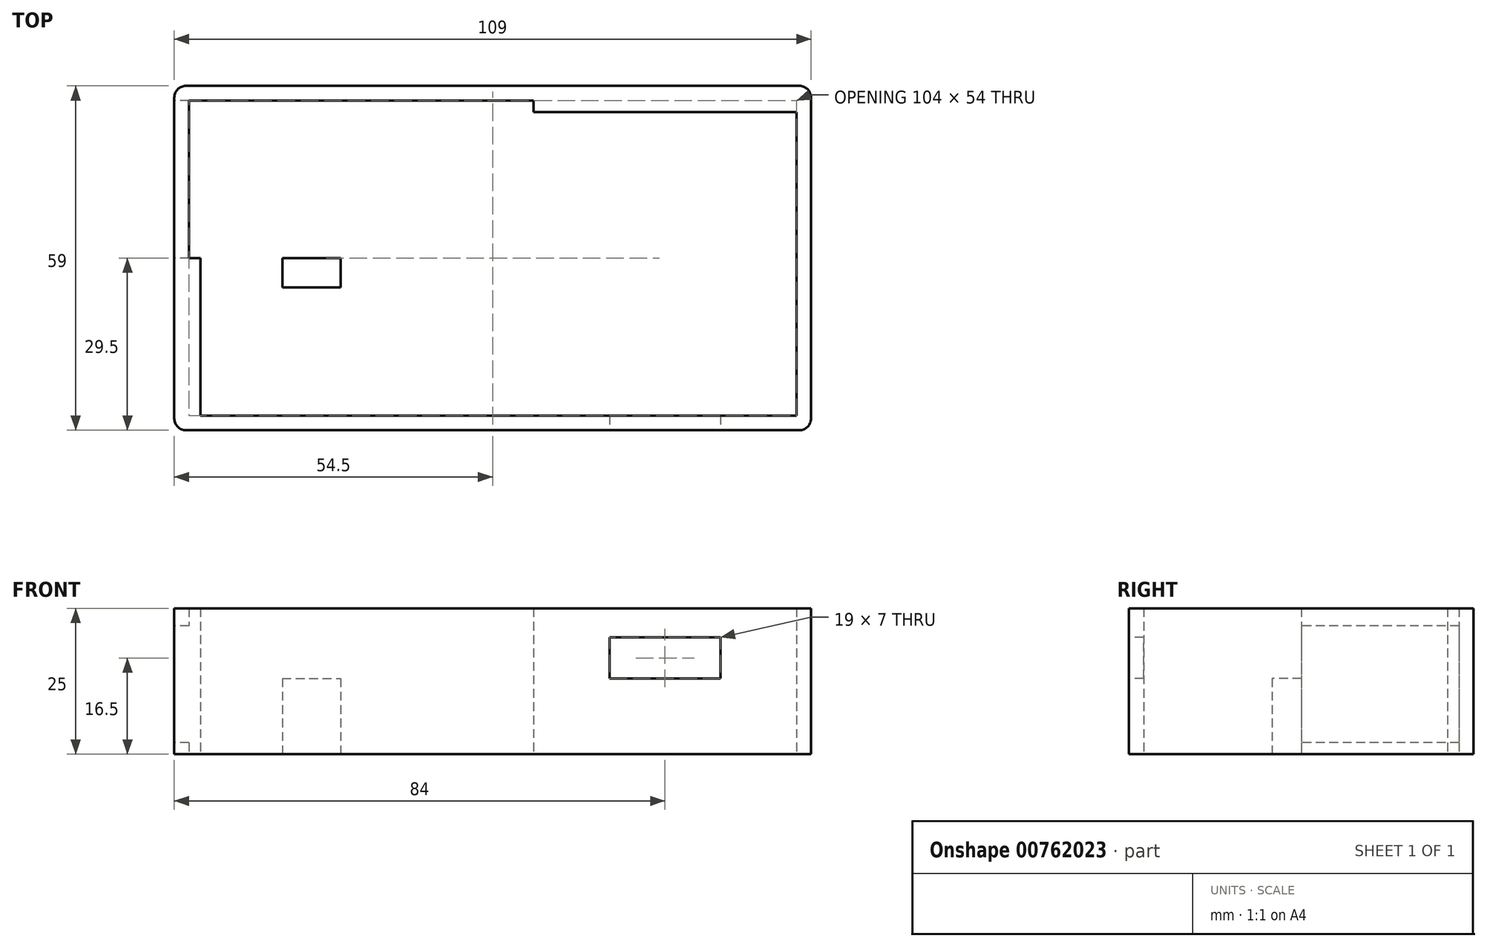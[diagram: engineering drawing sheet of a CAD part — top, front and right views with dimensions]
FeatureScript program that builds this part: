
annotation { "Feature Type Name" : "Feature", "Feature Type Description" : "" }
export const myFeature = defineFeature(function(context is Context, id is Id, definition is map)
    precondition{}
    {
        {
            var Q0;
            Q0=qCreatedBy(makeId("Top.planeOp"),FACE);
            var sketch = newSketch(context, id + "F0", { "sketchPlane" : qUnion([Q0])});
            skLineSegment(sketch, "E0.bottom", {"start": v(2, 0) * mm, "end": v(107, 0) * mm});
            skLineSegment(sketch, "E0.top", {"start": v(2, 59) * mm, "end": v(107, 59) * mm});
            skLineSegment(sketch, "E0.left", {"start": v(0, 2) * mm, "end": v(0, 57) * mm});
            skLineSegment(sketch, "E0.right", {"start": v(109, 2) * mm, "end": v(109, 57) * mm});
            skPoint(sketch, "E1.visualSharp", {"position": v(109, 59) * mm});
            skArc(sketch, "E1.filletArc", {"start": v(109, 57) * mm, "mid": v(108.41, 58.41) * mm, "end": v(107, 59) * mm});
            skPoint(sketch, "E2.visualSharp", {"position": v(109, 0) * mm});
            skArc(sketch, "E2.filletArc", {"start": v(107, 0) * mm, "mid": v(108.41, 0.59) * mm, "end": v(109, 2) * mm});
            skPoint(sketch, "E3.visualSharp", {"position": v(0, 0) * mm});
            skArc(sketch, "E3.filletArc", {"start": v(0, 2) * mm, "mid": v(0.59, 0.59) * mm, "end": v(2, 0) * mm});
            skPoint(sketch, "E4.visualSharp", {"position": v(0, 59) * mm});
            skArc(sketch, "E4.filletArc", {"start": v(2, 59) * mm, "mid": v(0.59, 58.41) * mm, "end": v(0, 57) * mm});
            skLineSegment(sketch, "E5.0", {"start": v(2.5, 56.5) * mm, "end": v(106.5, 56.5) * mm});
            skLineSegment(sketch, "E5.1", {"start": v(2.5, 2.5) * mm, "end": v(2.5, 56.5) * mm});
            skLineSegment(sketch, "E5.2", {"start": v(2.5, 2.5) * mm, "end": v(106.5, 2.5) * mm});
            skLineSegment(sketch, "E5.3", {"start": v(106.5, 2.5) * mm, "end": v(106.5, 56.5) * mm});
            skLineSegment(sketch, "E6.bottom", {"start": v(106.5, 56.5) * mm, "end": v(61.5, 56.5) * mm});
            skLineSegment(sketch, "E6.top", {"start": v(106.5, 54.5) * mm, "end": v(61.5, 54.5) * mm});
            skLineSegment(sketch, "E6.left", {"start": v(106.5, 56.5) * mm, "end": v(106.5, 54.5) * mm});
            skLineSegment(sketch, "E6.right", {"start": v(61.5, 56.5) * mm, "end": v(61.5, 54.5) * mm});
            skLineSegment(sketch, "E7.bottom", {"start": v(2.5, 2.5) * mm, "end": v(4.5, 2.5) * mm});
            skLineSegment(sketch, "E7.top", {"start": v(2.5, 29.5) * mm, "end": v(4.5, 29.5) * mm});
            skLineSegment(sketch, "E7.left", {"start": v(2.5, 2.5) * mm, "end": v(2.5, 29.5) * mm});
            skLineSegment(sketch, "E7.right", {"start": v(4.5, 2.5) * mm, "end": v(4.5, 29.5) * mm});
            skSolve(sketch);
        }
        {
            var Q0;
            Q0=makeQuery(id+"F0.imprint","IMPRINT",FACE,{"disambiguationData":[TD([[makeQuery(id+"F0.imprint","IMPRINT",EDGE,{"derivedFrom":sQuery(id+"F0.wireOp",EDGE,"E0.bottom")}),1.0]])]});
            extrude(context, id + "F1", {"entities" : qUnion([Q0]), "depth" : 25 * mm, "offsetDistance" : 25 * mm});
        }
        {
            var Q0;
            Q0=makeQuery(id+"F1.opExtrude","SWEPT_FACE",FACE,{"disambiguationData":[OSD([sQuery(id+"F0.wireOp",EDGE,"E0.bottom")])]});
            var sketch = newSketch(context, id + "F2", { "sketchPlane" : qUnion([Q0])});
            skLineSegment(sketch, "E8.bottom", {"start": v(74.5, 13) * mm, "end": v(93.5, 13) * mm});
            skLineSegment(sketch, "E8.top", {"start": v(74.5, 20) * mm, "end": v(93.5, 20) * mm});
            skLineSegment(sketch, "E8.left", {"start": v(74.5, 13) * mm, "end": v(74.5, 20) * mm});
            skLineSegment(sketch, "E8.right", {"start": v(93.5, 13) * mm, "end": v(93.5, 20) * mm});
            skSolve(sketch);
        }
        {
            var Q0;
            Q0 = qSketchRegion(id + "F2", true);
            extrude(context, id + "F3", {"entities" : qUnion([Q0]), "operationType" : NewBodyOperationType.REMOVE, "oppositeDirection" : true, "depth" : 2.5 * mm, "offsetDistance" : 25 * mm});
        }
        {
            var Q0;
            Q0=qCreatedBy(makeId("Top.planeOp"),FACE);
            var sketch = newSketch(context, id + "F4", { "sketchPlane" : qUnion([Q0])});
            skLineSegment(sketch, "E9.bottom", {"start": v(18.5, 29.5) * mm, "end": v(28.5, 29.5) * mm});
            skLineSegment(sketch, "E9.top", {"start": v(18.5, 24.5) * mm, "end": v(28.5, 24.5) * mm});
            skLineSegment(sketch, "E9.left", {"start": v(18.5, 29.5) * mm, "end": v(18.5, 24.5) * mm});
            skLineSegment(sketch, "E9.right", {"start": v(28.5, 29.5) * mm, "end": v(28.5, 24.5) * mm});
            skSolve(sketch);
        }
        {
            var Q0;
            {var subQ4=sQuery(id+"F0.wireOp",EDGE,"E6.top");Q0=makeQuery(id+"F0.imprint","IMPRINT",FACE,{"disambiguationData":[TD([[makeQuery(id+"F0.imprint","IMPRINT",EDGE,{"derivedFrom":subQ4}),-1.0]])]});}
            extrude(context, id + "F5", {"entities" : qUnion([Q0]), "operationType" : NewBodyOperationType.ADD, "depth" : 25 * mm, "offsetDistance" : 25 * mm});
        }
        {
            var Q0;
            {var subQ3=sQuery(id+"F0.wireOp",EDGE,"E7.top");Q0=makeQuery(id+"F0.imprint","IMPRINT",FACE,{"disambiguationData":[TD([[makeQuery(id+"F0.imprint","IMPRINT",EDGE,{"derivedFrom":subQ3}),-1.0]])]});}
            extrude(context, id + "F6", {"entities" : qUnion([Q0]), "operationType" : NewBodyOperationType.ADD, "depth" : 25 * mm, "offsetDistance" : 25 * mm});
        }
        {
            var Q0;
            Q0=makeQuery(id+"F4.imprint","IMPRINT",FACE,{"disambiguationData":[TD([[makeQuery(id+"F4.imprint","IMPRINT",EDGE,{"derivedFrom":sQuery(id+"F4.wireOp",EDGE,"E9.bottom")}),-1.0]])]});
            extrude(context, id + "F7", {"entities" : qUnion([Q0]), "operationType" : NewBodyOperationType.ADD, "depth" : 13 * mm, "offsetDistance" : 25 * mm});
        }
        {
            var Q0;
            Q0=makeQuery(id+"F1.opExtrude","SWEPT_FACE",FACE,{"disambiguationData":[OSD([sQuery(id+"F0.wireOp",EDGE,"E0.left")])]});
            var sketch = newSketch(context, id + "F8", { "sketchPlane" : qUnion([Q0])});
            skLineSegment(sketch, "E10.bottom", {"start": v(-56.5, 22) * mm, "end": v(-29.5, 22) * mm});
            skLineSegment(sketch, "E10.top", {"start": v(-56.5, 2) * mm, "end": v(-29.5, 2) * mm});
            skLineSegment(sketch, "E10.left", {"start": v(-56.5, 22) * mm, "end": v(-56.5, 2) * mm});
            skLineSegment(sketch, "E10.right", {"start": v(-29.5, 22) * mm, "end": v(-29.5, 2) * mm});
            skSolve(sketch);
        }
        {
            var Q0;
            Q0 = qSketchRegion(id + "F8", true);
            extrude(context, id + "F9", {"entities" : qUnion([Q0]), "operationType" : NewBodyOperationType.REMOVE, "oppositeDirection" : true, "depth" : 2.5 * mm, "offsetDistance" : 25 * mm});
        }
        {
            var Q0;
            Q0=makeQuery(id+"F4.imprint","IMPRINT",FACE,{"disambiguationData":[TD([[makeQuery(id+"F4.imprint","IMPRINT",EDGE,{"derivedFrom":sQuery(id+"F4.wireOp",EDGE,"E9.bottom")}),-1.0]])]});
            extrude(context, id + "F10", {"entities" : qUnion([Q0]), "depth" : 13 * mm, "offsetDistance" : 25 * mm});
        }
    });
